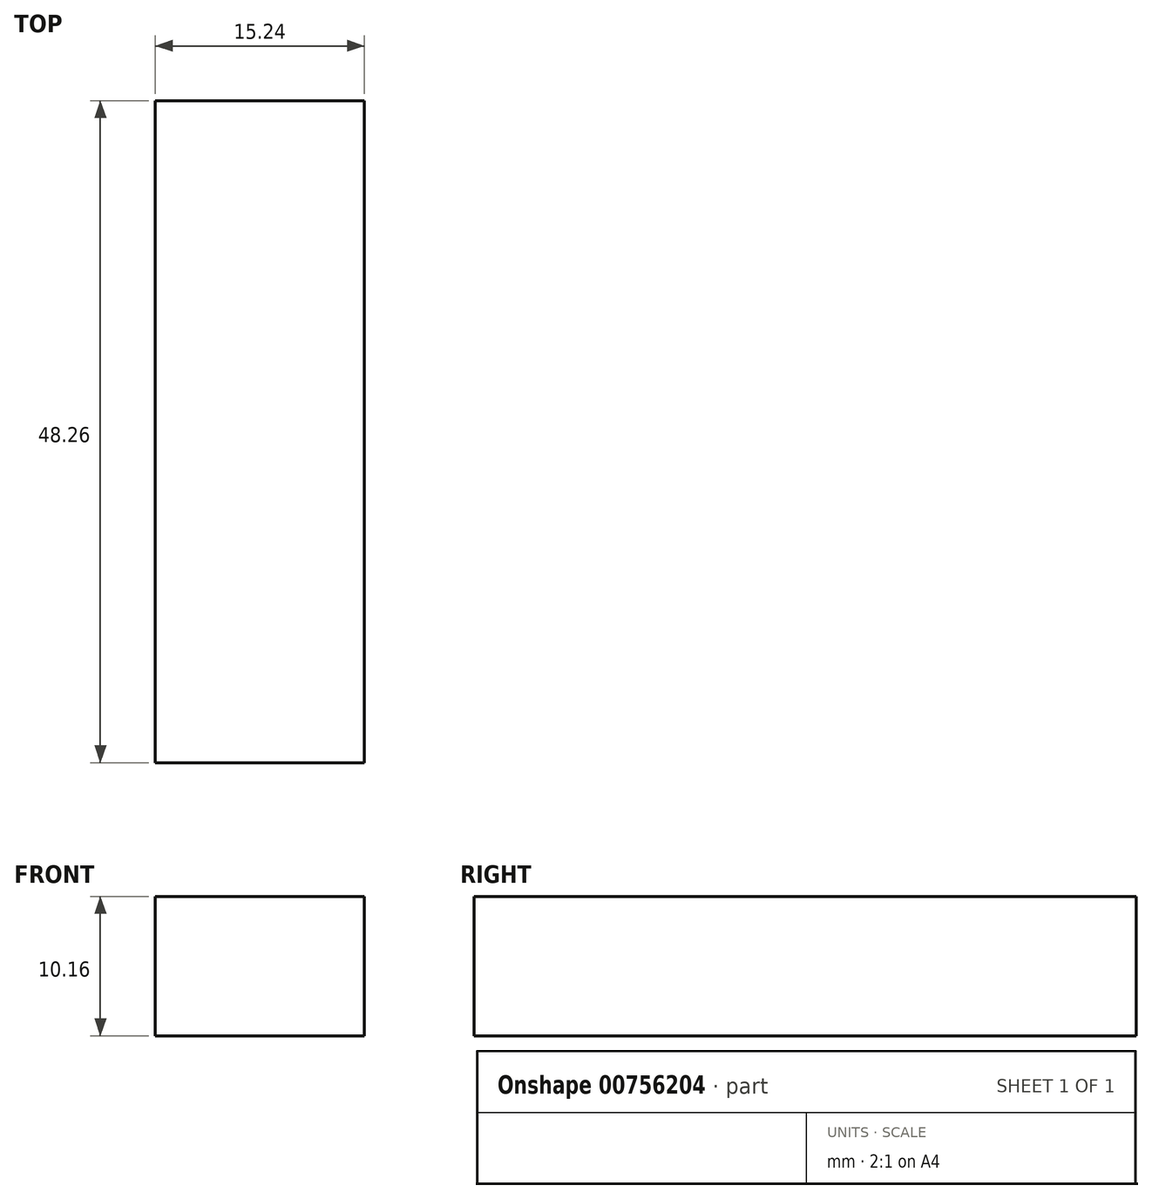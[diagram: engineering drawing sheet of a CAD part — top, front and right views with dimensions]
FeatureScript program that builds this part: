
annotation { "Feature Type Name" : "Feature", "Feature Type Description" : "" }
export const myFeature = defineFeature(function(context is Context, id is Id, definition is map)
    precondition{}
    {
        {
            var Q0;
            Q0=qCreatedBy(makeId("Top.planeOp"),FACE);
            var sketch = newSketch(context, id + "F0", { "sketchPlane" : qUnion([Q0])});
            skLineSegment(sketch, "E0.bottom", {"start": v(-7.62, 24.13) * mm, "end": v(7.62, 24.13) * mm});
            skLineSegment(sketch, "E0.top", {"start": v(-7.62, -24.13) * mm, "end": v(7.62, -24.13) * mm});
            skLineSegment(sketch, "E0.left", {"start": v(-7.62, 24.13) * mm, "end": v(-7.62, -24.13) * mm});
            skLineSegment(sketch, "E0.right", {"start": v(7.62, 24.13) * mm, "end": v(7.62, -24.13) * mm});
            skPoint(sketch, "E0.middle", {"position": v(0, 0) * mm});
            skSolve(sketch);
        }
        {
            var Q0;
            Q0 = qSketchRegion(id + "F0", true);
            extrude(context, id + "F1", {"entities" : qUnion([Q0]), "depth" : 10.16 * mm, "offsetDistance" : 25 * mm});
        }
    });
